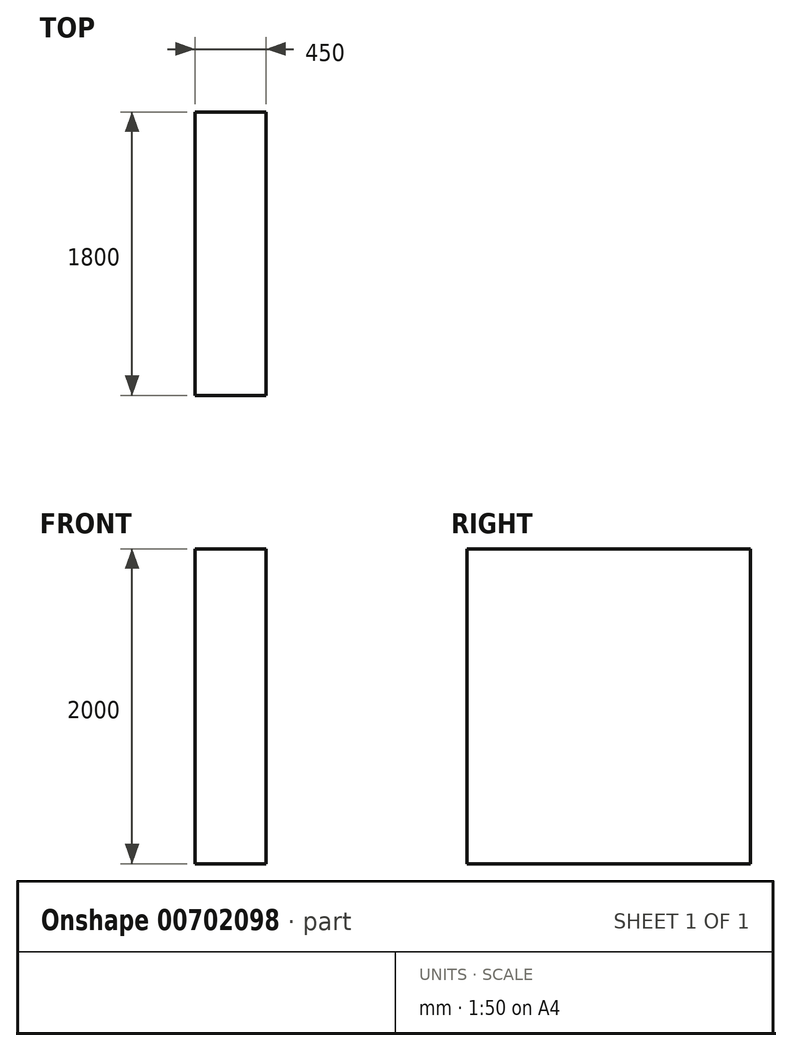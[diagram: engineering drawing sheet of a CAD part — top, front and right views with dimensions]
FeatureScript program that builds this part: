
annotation { "Feature Type Name" : "Feature", "Feature Type Description" : "" }
export const myFeature = defineFeature(function(context is Context, id is Id, definition is map)
    precondition{}
    {
        {
            var Q0;
            Q0=qCreatedBy(makeId("Top.planeOp"),FACE);
            var sketch = newSketch(context, id + "F0", { "sketchPlane" : qUnion([Q0])});
            skLineSegment(sketch, "E0.bottom", {"start": v(0, 0) * mm, "end": v(450, 0) * mm});
            skLineSegment(sketch, "E0.top", {"start": v(0, 1800) * mm, "end": v(450, 1800) * mm});
            skLineSegment(sketch, "E0.left", {"start": v(0, 0) * mm, "end": v(0, 1800) * mm});
            skLineSegment(sketch, "E0.right", {"start": v(450, 0) * mm, "end": v(450, 1800) * mm});
            skSolve(sketch);
        }
        {
            var Q0;
            Q0=makeQuery(id+"F0.imprint","IMPRINT",FACE,{"disambiguationData":[TD([[makeQuery(id+"F0.imprint","IMPRINT",EDGE,{"derivedFrom":sQuery(id+"F0.wireOp",EDGE,"E0.bottom")}),1.0]])]});
            extrude(context, id + "F1", {"entities" : qUnion([Q0]), "depth" : 2000 * mm, "offsetDistance" : 25 * mm});
        }
    });
